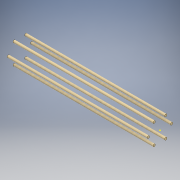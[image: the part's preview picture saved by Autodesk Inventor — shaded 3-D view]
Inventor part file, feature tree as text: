
AUTODESK INVENTOR PART (.ipt)
format: ipt  version: 2017.3 (Build 213256000, 256)  size: 129,024 bytes
history: native  units: mm
features: sketch x4, extrude x3
ambient origin geometry x8: Origin, YZ Plane, XZ Plane, XY Plane, X Axis, Y Axis, Z Axis, Center Point
bodies: Solid1 (feature_tree)
feature tree (7):
  extrude  "Extrusion1"  Depth=1.0mm TaperAngle=0.0deg
  extrude  "Extrusion2"  Depth=1.6mm
  sketch  "Sketch3"  dims[d6=1.6mm d7=1.6mm]
  extrude  "Extrusion3"  Depth=1.6mm
  sketch  "Sketch1"  dims[d0=19.0mm d1=1.0mm d2=0.0mm]
  sketch  "Sketch2"  dims[d4=1.6mm d5=1.6mm]
  sketch  "Sketch4"  dims[d8=1.6mm d9=1.6mm d10=99.0mm d11=0.0mm d12=6.0mm d13=0.0mm]
